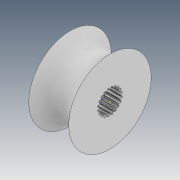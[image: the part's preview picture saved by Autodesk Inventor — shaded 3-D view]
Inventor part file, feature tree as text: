
AUTODESK INVENTOR PART (.ipt)
format: ipt  version: 2021 (Build 250183000, 183)  size: 327,168 bytes
history: native  units: in
note: dims shown in document units (in); Inventor stores cm internally (conversion verified against a paired STEP export)
features: other x2, sketch x2, extrude x1
ambient origin geometry x8: Origin, YZ Plane, XZ Plane, XY Plane, X Axis, Y Axis, Z Axis, Center Point
bodies: Body1 (feature_tree)
feature tree (5):
  other  "Sólido1"
  other  "Revolução1"
  extrude  "Extrusão5"  Depth=0.3858in
  sketch  "Esboço12"  dims[d0=0.374in d1=0.3858in]
  sketch  "Esboço13"  dims[d2=90.0deg d58=0.2008in d59=0.2323in d60=0.0024in d61=0.0024in d62=0.002in d63=0.002in d64=7.874in d66=360.0deg d68=0.1378in d69=0.0in d70=0.2165in]
